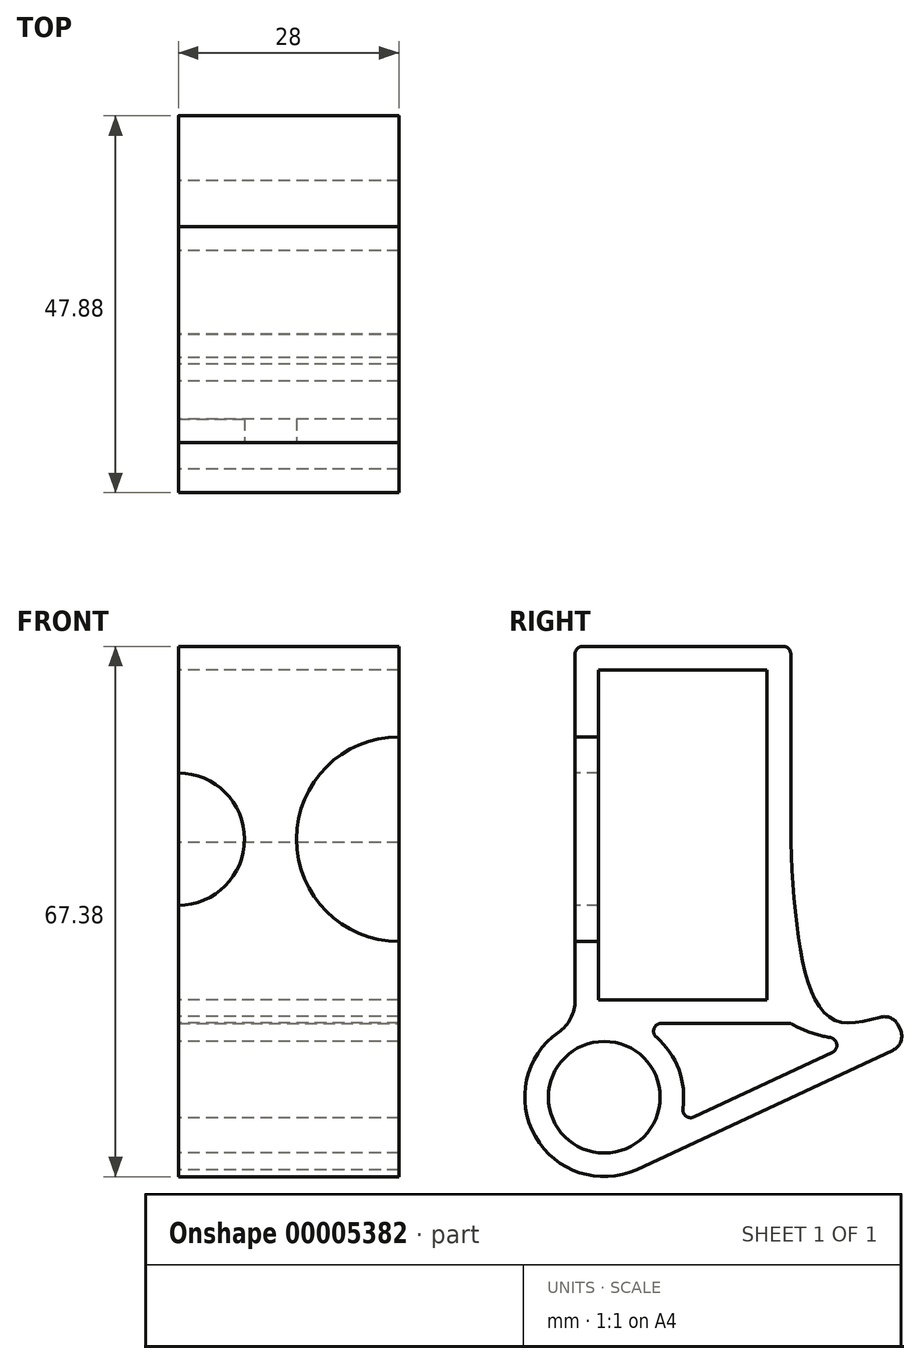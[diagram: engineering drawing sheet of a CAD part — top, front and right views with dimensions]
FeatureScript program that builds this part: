
annotation { "Feature Type Name" : "Feature", "Feature Type Description" : "" }
export const myFeature = defineFeature(function(context is Context, id is Id, definition is map)
    precondition{}
    {
        {
            var Q0;
            Q0=qCreatedBy(makeId("Right.planeOp"),FACE);
            var sketch = newSketch(context, id + "F0", { "sketchPlane" : qUnion([Q0])});
            skLineSegment(sketch, "E0.bottom", {"start": v(-19.41, 23.63) * mm, "end": v(1.99, 23.63) * mm});
            skLineSegment(sketch, "E0.top", {"start": v(-19.41, -18.27) * mm, "end": v(1.99, -18.27) * mm});
            skLineSegment(sketch, "E0.left", {"start": v(-19.41, 23.63) * mm, "end": v(-19.41, -18.27) * mm});
            skLineSegment(sketch, "E0.right", {"start": v(1.99, 23.63) * mm, "end": v(1.99, -18.27) * mm});
            skLineSegment(sketch, "E1.0", {"start": v(-22.41, 26.63) * mm, "end": v(4.99, 26.63) * mm});
            skLineSegment(sketch, "E1.1", {"start": v(-22.41, 26.63) * mm, "end": v(-22.41, -21.27) * mm});
            skLineSegment(sketch, "E1.2", {"start": v(-22.41, -21.27) * mm, "end": v(4.99, -21.27) * mm});
            skLineSegment(sketch, "E1.3", {"start": v(4.99, 26.63) * mm, "end": v(4.99, -21.27) * mm});
            skLineSegment(sketch, "E2", {"start": v(-15.55, -37.01) * mm, "end": v(24.38, -18.4) * mm});
            skLineSegment(sketch, "E3.0", {"start": v(-14.28, -39.73) * mm, "end": v(25.16, -21.33) * mm});
            skLineSegment(sketch, "E4", {"start": v(-15.55, -37.01) * mm, "end": v(-26.5, -42.12) * mm});
            skLineSegment(sketch, "E5", {"start": v(-14.28, -39.73) * mm, "end": v(-33.69, -48.78) * mm});
            skFitSpline(sketch, "E6", {"points": [v(4.99, 1.73) * mm, v(10.15, -20.66) * mm, v(24.38, -18.4) * mm], "startDerivative": vector(2.28, -51.5) * mm, "endDerivative": vector(40.88, 5.87) * mm});
            skFitSpline(sketch, "E7", {"points": [v(4.99, -21.27) * mm, v(14.07, -23.2) * mm, v(25.16, -21.33) * mm], "startDerivative": vector(20.3, -11.77) * mm, "endDerivative": vector(23.73, 4.93) * mm});
            skLineSegment(sketch, "E8", {"start": v(24.38, -18.4) * mm, "end": v(25.16, -21.33) * mm});
            skCircle(sketch, "E9", {"center": v(-18.7, -30.65) * mm, "radius": 10.1 * mm});
            skPoint(sketch, "E9.third.point", {"position": v(-26.5, -37.05) * mm});
            skCircle(sketch, "E10.0", {"center": v(-18.7, -30.65) * mm, "radius": 7.1 * mm});
            skLineSegment(sketch, "E11", {"start": v(17.95, -20) * mm, "end": v(19.75, -23.86) * mm});
            skSolve(sketch);
        }
        {
            var Q0;
            {var subQ1=sQuery(id+"F0.wireOp",EDGE,"E4");var subQ5=sQuery(id+"F0.wireOp",EDGE,"E2");var subQ11=makeQuery(id+"F0.imprint","INTERSECT",VERTEX,{"derivedFrom":[subQ5,subQ1]});Q0=makeQuery(id+"F0.imprint","IMPRINT",FACE,{"disambiguationData":[TD([[makeQuery(id+"F0.imprint","IMPRINT",EDGE,{"disambiguationData":[TD([[subQ11,-1.0]])],"derivedFrom":subQ5}),1.0]])]});}
            var Q1;
            Q1=makeQuery(id+"F0.imprint","IMPRINT",FACE,{"disambiguationData":[TD([[makeQuery(id+"F0.imprint","IMPRINT",EDGE,{"derivedFrom":sQuery(id+"F0.wireOp",EDGE,"E0.bottom")}),1.0]])]});
            var Q2;
            {var subQ1=sQuery(id+"F0.wireOp",EDGE,"E4");var subQ5=sQuery(id+"F0.wireOp",EDGE,"E2");var subQ11=makeQuery(id+"F0.imprint","INTERSECT",VERTEX,{"derivedFrom":[subQ5,subQ1]});Q2=makeQuery(id+"F0.imprint","IMPRINT",FACE,{"disambiguationData":[TD([[makeQuery(id+"F0.imprint","IMPRINT",EDGE,{"disambiguationData":[TD([[subQ11,-1.0]])],"derivedFrom":subQ5}),-1.0]])]});}
            var Q3;
            {var subQ0=sQuery(id+"F0.wireOp",EDGE,"E9");var subQ1=sQuery(id+"F0.wireOp",EDGE,"E1.2");var subQ2=makeQuery(id+"F0.imprint","INTERSECT",VERTEX,{"derivedFrom":[subQ1,subQ0]});Q3=makeQuery(id+"F0.imprint","IMPRINT",FACE,{"disambiguationData":[TD([[makeQuery(id+"F0.imprint","IMPRINT",EDGE,{"disambiguationData":[TD([[subQ2,1.0]])],"derivedFrom":subQ1}),1.0]])]});}
            var Q4;
            {var subQ5=sQuery(id+"F0.wireOp",EDGE,"E9");var subQ6=sQuery(id+"F0.wireOp",EDGE,"E2");var subQ7=makeQuery(id+"F0.imprint","INTERSECT",VERTEX,{"derivedFrom":[subQ6,subQ5]});Q4=makeQuery(id+"F0.imprint","IMPRINT",FACE,{"disambiguationData":[TD([[makeQuery(id+"F0.imprint","IMPRINT",EDGE,{"disambiguationData":[TD([[subQ7,-1.0]])],"derivedFrom":subQ6}),-1.0]])]});}
            var Q5;
            {var subQ1=sQuery(id+"F0.wireOp",EDGE,"E2");var subQ5=sQuery(id+"F0.wireOp",EDGE,"E7");var subQ6=makeQuery(id+"F0.imprint","INTERSECT",VERTEX,{"derivedFrom":[subQ1,subQ5]});Q5=makeQuery(id+"F0.imprint","IMPRINT",FACE,{"disambiguationData":[TD([[makeQuery(id+"F0.imprint","IMPRINT",EDGE,{"disambiguationData":[TD([[subQ6,-1.0]])],"derivedFrom":subQ1}),1.0]])]});}
            var Q6;
            {var subQ1=sQuery(id+"F0.wireOp",EDGE,"E7");var subQ3=sQuery(id+"F0.wireOp",EDGE,"E2");var subQ5=makeQuery(id+"F0.imprint","INTERSECT",VERTEX,{"derivedFrom":[subQ3,subQ1]});Q6=makeQuery(id+"F0.imprint","IMPRINT",FACE,{"disambiguationData":[TD([[makeQuery(id+"F0.imprint","IMPRINT",EDGE,{"disambiguationData":[TD([[subQ5,-1.0]])],"derivedFrom":subQ3}),-1.0]])]});}
            extrude(context, id + "F1", {"entities" : qUnion([Q0, Q1, Q2, Q3, Q4, Q5, Q6]), "depth" : 28 * mm});
        }
        {
            var Q0;
            Q0=makeQuery(id+"F1.opExtrude","SWEPT_FACE",FACE,{"disambiguationData":[OSD([sQuery(id+"F0.wireOp",EDGE,"E1.1")])]});
            var sketch = newSketch(context, id + "F2", { "sketchPlane" : qUnion([Q0])});
            skLineSegment(sketch, "E12", {"start": v(0, 23.63) * mm, "end": v(28, 23.63) * mm});
            skCircle(sketch, "E13", {"center": v(28, 2.13) * mm, "radius": 13 * mm});
            skCircle(sketch, "E14", {"center": v(0, 2.13) * mm, "radius": 8.4 * mm});
            skSolve(sketch);
        }
        {
            var Q0;
            Q0=qSketchRegion(id+"F2",true);
            extrude(context, id + "F3", {"entities" : qUnion([Q0]), "operationType" : NewBodyOperationType.REMOVE, "oppositeDirection" : true, "depth" : 3 * mm});
        }
        {
            var Q0;
            Q0=makeQuery(id+"F1.opExtrude","SWEPT_EDGE",EDGE,{"disambiguationData":[OSD([sQuery(id+"F0.wireOp",EDGE,"E6"),sQuery(id+"F0.wireOp",EDGE,"E11")])]});
            var Q1;
            Q1=makeQuery(id+"F1.opExtrude","SWEPT_EDGE",EDGE,{"disambiguationData":[OSD([sQuery(id+"F0.wireOp",EDGE,"E3.0"),sQuery(id+"F0.wireOp",EDGE,"E11")])]});
            fillet(context, id + "F4", {"entities" : qUnion([Q0, Q1]), "radius" : 2 * mm, "tangentPropagation" : true, "allowEdgeOverflow" : false});
        }
        {
            var Q0;
            Q0=makeQuery(id+"F1.opExtrude","SWEPT_EDGE",EDGE,{"disambiguationData":[OSD([sQuery(id+"F0.wireOp",EDGE,"E1.1"),sQuery(id+"F0.wireOp",EDGE,"E1.2"),sQuery(id+"F0.wireOp",EDGE,"E9")])]});
            fillet(context, id + "F5", {"entities" : qUnion([Q0]), "radius" : 5 * mm, "tangentPropagation" : true, "allowEdgeOverflow" : false});
        }
        {
            var Q0;
            Q0=makeQuery(id+"F1.opExtrude","SWEPT_EDGE",EDGE,{"disambiguationData":[OSD([sQuery(id+"F0.wireOp",EDGE,"E2"),sQuery(id+"F0.wireOp",EDGE,"E7")])]});
            var Q1;
            Q1=makeQuery(id+"F1.opExtrude","SWEPT_EDGE",EDGE,{"disambiguationData":[OSD([sQuery(id+"F0.wireOp",EDGE,"E1.2"),sQuery(id+"F0.wireOp",EDGE,"E9")])]});
            var Q2;
            Q2=makeQuery(id+"F1.opExtrude","SWEPT_EDGE",EDGE,{"disambiguationData":[OSD([sQuery(id+"F0.wireOp",EDGE,"E2"),sQuery(id+"F0.wireOp",EDGE,"E9")])]});
            fillet(context, id + "F6", {"entities" : qUnion([Q0, Q1, Q2]), "radius" : 1 * mm, "tangentPropagation" : true, "allowEdgeOverflow" : false});
        }
        {
            var Q0;
            Q0=makeQuery(id+"F1.opExtrude","SWEPT_EDGE",EDGE,{"disambiguationData":[OSD([sQuery(id+"F0.wireOp",EDGE,"E1.0"),sQuery(id+"F0.wireOp",EDGE,"E1.1")])]});
            var Q1;
            Q1=makeQuery(id+"F1.opExtrude","SWEPT_EDGE",EDGE,{"disambiguationData":[OSD([sQuery(id+"F0.wireOp",EDGE,"E1.0"),sQuery(id+"F0.wireOp",EDGE,"E1.3")])]});
            fillet(context, id + "F7", {"entities" : qUnion([Q0, Q1]), "radius" : 1 * mm, "tangentPropagation" : true, "allowEdgeOverflow" : false});
        }
    });
